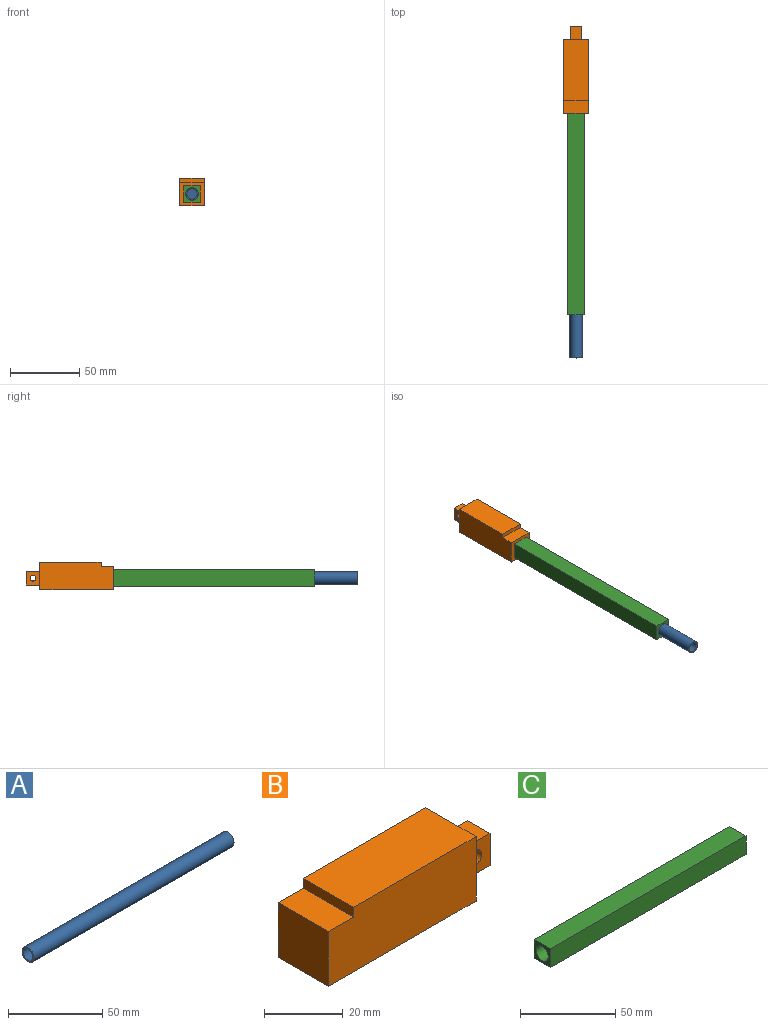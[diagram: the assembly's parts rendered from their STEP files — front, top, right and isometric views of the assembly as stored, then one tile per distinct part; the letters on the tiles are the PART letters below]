
ASSEMBLY  parts=3 mates=2
PART A: 5 faces, bbox 150x9x9 mm
  f0: plane 7.46x7.46mm, normal (-1,0,0), area 43.7mm2, adj f1
  f1: cylinder r=3.73mm len=149.23mm, axis (1,0,0), area 3497.4mm2, adj f0,f2
  f2: plane 9x9mm, normal (-1,0,0), area 19.9mm2, adj f1,f4
  f3: plane 9x9mm, normal (1,0,0), area 63.6mm2, adj f4
  f4: cylinder r=4.5mm len=150mm, axis (1,0,0), area 4241.2mm2, adj f2,f3
PART B: 14 faces, bbox 63x18x20 mm
  f0: plane 20x18mm, normal (1,0,0), area 280mm2, adj f3,f4,f6,f7,f8,f9,f12,f13
  f1: plane 18x9mm, normal (0,0,1), area 162mm2, adj f2,f5,f6,f7
  f2: plane 18x17mm, normal (-1,0,0), area 306mm2, adj f1,f3,f6,f7
  f3: plane 53x18mm, normal (0,0,-1), area 954mm2, adj f0,f2,f6,f7
  f4: plane 44x18mm, normal (0,0,1), area 792mm2, adj f0,f5,f6,f7
  f5: plane 18x3mm, normal (-1,0,0), area 54mm2, adj f1,f4,f6,f7
  f6: plane 53x20mm, normal (0,-1,0), area 1033mm2, adj f0,f1,f2,f3,f4,f5
  f7: plane 53x20mm, normal (0,1,0), area 1033mm2, adj f0,f1,f2,f3,f4,f5
  f8: plane 10x8mm, normal (0,0,1), area 80mm2, adj f0,f11,f12,f13
  f9: plane 10x8mm, normal (0,0,-1), area 80mm2, adj f0,f11,f12,f13
  f10: cylinder r=2.12mm len=8mm, axis (0,1,0), area 106.8mm2, adj f12,f13
  f11: plane 10x8mm, normal (1,0,0), area 80mm2, adj f8,f9,f12,f13
  f12: plane 10x10mm, normal (0,-1,0), area 85.8mm2, adj f0,f8,f9,f10,f11
  f13: plane 10x10mm, normal (0,1,0), area 85.8mm2, adj f0,f8,f9,f10,f11
PART C: 7 faces, bbox 145x12x12 mm
  f0: plane 145x12mm, normal (0,-1,0), area 1740mm2, adj f1,f3,f5,f6
  f1: plane 145x12mm, normal (0,0,1), area 1740mm2, adj f0,f2,f5,f6
  f2: plane 145x12mm, normal (0,1,0), area 1740mm2, adj f1,f3,f5,f6
  f3: plane 145x12mm, normal (0,0,-1), area 1740mm2, adj f0,f2,f5,f6
  f4: cylinder r=4.5mm len=145mm, axis (1,0,0), area 4099.8mm2, adj f5,f6
  f5: plane 12x12mm, normal (-1,0,0), area 80.4mm2, adj f0,f1,f2,f3,f4
  f6: plane 12x12mm, normal (1,0,0), area 80.4mm2, adj f0,f1,f2,f3,f4
PLACE A rot(axis=(-0.71,-0.71,0),180deg) t=(0,0.46,-1.5)mm
PLACE B rot(axis=(0,0,1),90deg) t=(0,26.5,1.5)mm
PLACE C rot(axis=(-0.58,-0.58,0.58),120deg) t=(-1.5,26.5,0)mm
MATE slider C.f4 <-> A.f1  axis (0,-1,0) through (0,-145,0)mm
MATE fastened B.f2 <-> C.f4  axis (0,-1,0) through (0,0,0)mm
